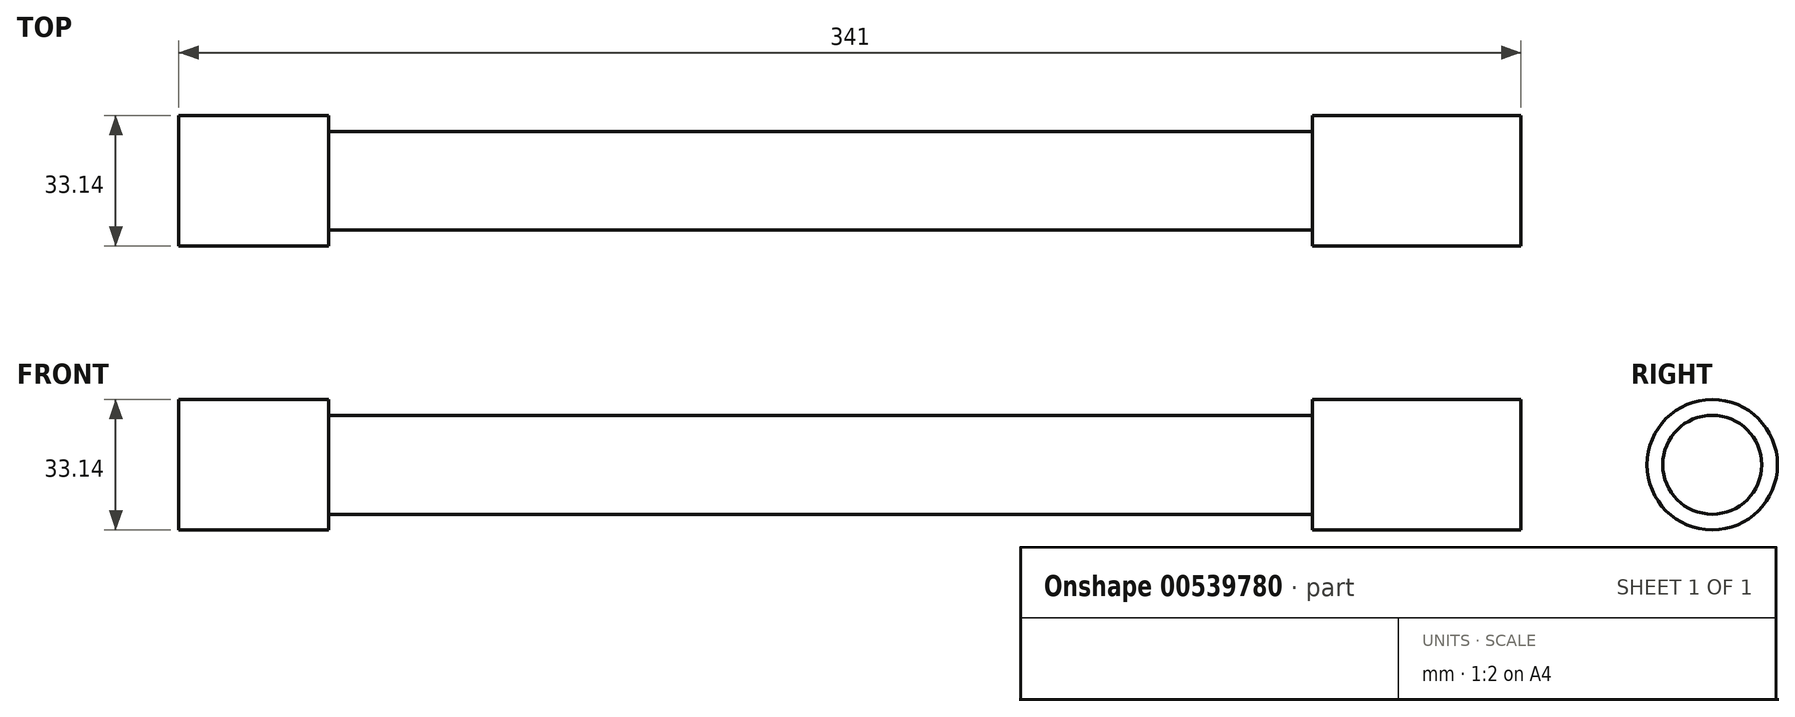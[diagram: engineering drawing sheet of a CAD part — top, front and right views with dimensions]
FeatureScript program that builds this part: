
annotation { "Feature Type Name" : "Feature", "Feature Type Description" : "" }
export const myFeature = defineFeature(function(context is Context, id is Id, definition is map)
    precondition{}
    {
        {
            var Q0;
            Q0=qCreatedBy(makeId("Top.planeOp"),FACE);
            var sketch = newSketch(context, id + "F0", { "sketchPlane" : qUnion([Q0])});
            skLineSegment(sketch, "E0.bottom", {"start": v(-60, 11.28) * mm, "end": v(0, 11.28) * mm});
            skLineSegment(sketch, "E0.top", {"start": v(-60, 8.28) * mm, "end": v(0, 8.28) * mm});
            skLineSegment(sketch, "E0.left", {"start": v(-60, 11.28) * mm, "end": v(-60, 8.28) * mm});
            skLineSegment(sketch, "E0.right", {"start": v(0, 11.28) * mm, "end": v(0, 8.28) * mm});
            skLineSegment(sketch, "E1.bottom", {"start": v(0, 8.28) * mm, "end": v(3, 8.28) * mm});
            skLineSegment(sketch, "E1.top", {"start": v(0, 23.28) * mm, "end": v(3, 23.28) * mm});
            skLineSegment(sketch, "E1.left", {"start": v(0, 8.28) * mm, "end": v(0, 23.28) * mm});
            skLineSegment(sketch, "E1.right", {"start": v(3, 8.28) * mm, "end": v(3, 23.28) * mm});
            skSolve(sketch);
        }
        {
            var Q0;
            Q0=qCreatedBy(makeId("Top.planeOp"),FACE);
            var sketch = newSketch(context, id + "F1", { "sketchPlane" : qUnion([Q0])});
            skLineSegment(sketch, "E2", {"start": v(12.6, 0) * mm, "end": v(-275.4, 0) * mm});
            skLineSegment(sketch, "E3", {"start": v(-275.4, 0) * mm, "end": v(-275.4, 16.5) * mm});
            skLineSegment(sketch, "E4", {"start": v(-275.4, 16.5) * mm, "end": v(-237.4, 16.5) * mm});
            skLineSegment(sketch, "E5", {"start": v(-237.4, 0) * mm, "end": v(-275.4, 0) * mm});
            skLineSegment(sketch, "E6", {"start": v(65.6, 16.5) * mm, "end": v(12.6, 16.5) * mm});
            skLineSegment(sketch, "E7", {"start": v(12.6, 16.5) * mm, "end": v(12.6, 12.5) * mm});
            skLineSegment(sketch, "E8", {"start": v(12.6, 0) * mm, "end": v(65.6, 0) * mm});
            skLineSegment(sketch, "E9", {"start": v(65.6, 16.5) * mm, "end": v(65.6, 0) * mm});
            skLineSegment(sketch, "E10", {"start": v(12.6, 12.5) * mm, "end": v(-237.4, 12.5) * mm});
            skLineSegment(sketch, "E11.bottom", {"start": v(-274.7, -0.07) * mm, "end": v(-238.45, -0.07) * mm});
            skLineSegment(sketch, "E12.bottom", {"start": v(-274.7, -0.07) * mm, "end": v(-275.4, -0.07) * mm});
            skLineSegment(sketch, "E12.right", {"start": v(-275.4, -0.07) * mm, "end": v(-275.4, 15.5) * mm});
            skLineSegment(sketch, "E13.bottom", {"start": v(-237.4, 16.5) * mm, "end": v(-237.4, 16.5) * mm});
            skLineSegment(sketch, "E13.top", {"start": v(-237.4, 12.5) * mm, "end": v(-237.4, 12.5) * mm});
            skLineSegment(sketch, "E13.left", {"start": v(-237.4, 16.5) * mm, "end": v(-237.4, 12.5) * mm});
            skLineSegment(sketch, "E13.right", {"start": v(-237.4, 16.5) * mm, "end": v(-237.4, 12.5) * mm});
            skLineSegment(sketch, "E14.bottom", {"start": v(12.6, 0) * mm, "end": v(65.4, 0) * mm});
            skSolve(sketch);
        }
        {
            var Q0;
            Q0=sQuery(id+"F1.wireOp",EDGE,"E4");
            var Q1;
            Q1=sQuery(id+"F1.wireOp",EDGE,"E10");
            var Q2;
            Q2=sQuery(id+"F1.wireOp",EDGE,"E6");
            var Q3;
            Q3=sQuery(id+"F1.wireOp",EDGE,"E13.left");
            var Q4;
            Q4=sQuery(id+"F1.wireOp",EDGE,"E7");
            var Q5;
            Q5=sQuery(id+"F1.wireOp",EDGE,"E11.bottom");
            revolve(context, id + "F2", {"bodyType" : ToolBodyType.SURFACE, "surfaceOperationType" : NewSurfaceOperationType.NEW, "surfaceEntities" : qUnion([Q0, Q1, Q2, Q3, Q4]), "axis" : qUnion([Q5]), "revolveType" : RevolveType.FULL});
        }
    });
